# Revit family: QF_COMCATER ALL BRANDS_RCSTD3.201214112601
name_source: partatom
category: Specialty Equipment
revit_build: Autodesk Revit 2016 (Build: 20150220_1215(x64)
units: mm (PartAtom-declared; Revit-internal decimal feet)

## family parameters
Always vertical = Yes
Cut with Voids When Loaded = No
OmniClass Number = 23.40.40.14
OmniClass Title = Food Service Equipment
Part Type = Normal
Room Calculation Point = No
Round Connector Dimension = Use Diameter
Shared = No
Work Plane-Based = No

## types (1)
- RCSTD3
    Accessory = No
    Cost = 0 $
    Depth Actual = 683 mm  [stored 2.24081 ft]
    Description = 300MM WIDE STANDS
    Height Actual = 680 mm  [stored 2.23097 ft]
    Length Actual = 300 mm
    Manufacturer = TRUEHEAT
    Model = RCSTD3
    URL = www.comcater.com.au
    Weight = 7.80 kg

note: [stored X ft] marks values corroborated as IEEE doubles in the binary element streams (Revit-internal decimal feet)

## geometry (parser evidence)
native form markers: Sweep x5
no freeform markers — native parametric forms only
